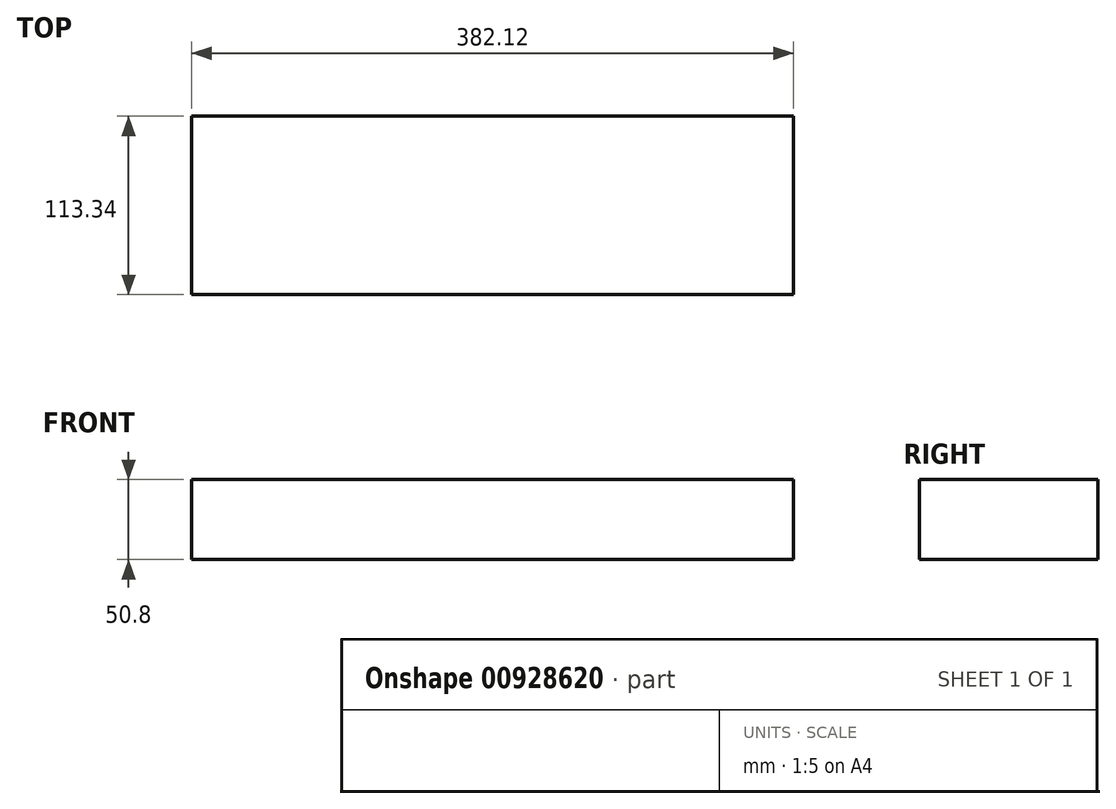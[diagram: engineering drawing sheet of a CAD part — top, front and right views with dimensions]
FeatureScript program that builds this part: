
annotation { "Feature Type Name" : "Feature", "Feature Type Description" : "" }
export const myFeature = defineFeature(function(context is Context, id is Id, definition is map)
    precondition{}
    {
        {
            var Q0;
            Q0=qCreatedBy(makeId("Top.planeOp"),FACE);
            var sketch = newSketch(context, id + "F0", { "sketchPlane" : qUnion([Q0])});
            skLineSegment(sketch, "E0.bottom", {"start": v(191.06, -56.67) * mm, "end": v(-191.06, -56.67) * mm});
            skLineSegment(sketch, "E0.top", {"start": v(191.06, 56.67) * mm, "end": v(-191.06, 56.67) * mm});
            skLineSegment(sketch, "E0.left", {"start": v(191.06, -56.67) * mm, "end": v(191.06, 56.67) * mm});
            skLineSegment(sketch, "E0.right", {"start": v(-191.06, -56.67) * mm, "end": v(-191.06, 56.67) * mm});
            skPoint(sketch, "E0.middle", {"position": v(0, 0) * mm});
            skSolve(sketch);
        }
        {
            var Q0;
            Q0=makeQuery(id+"F0.imprint","IMPRINT",FACE,{"disambiguationData":[TD([[makeQuery(id+"F0.imprint","IMPRINT",EDGE,{"derivedFrom":sQuery(id+"F0.wireOp",EDGE,"E0.bottom")}),-1.0]])]});
            extrude(context, id + "F1", {"entities" : qUnion([Q0]), "depth" : 50.8 * mm, "offsetDistance" : 25.4 * mm});
        }
    });
